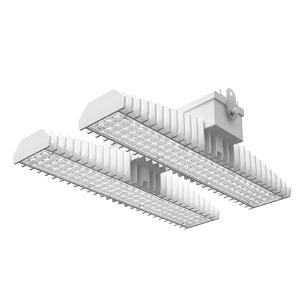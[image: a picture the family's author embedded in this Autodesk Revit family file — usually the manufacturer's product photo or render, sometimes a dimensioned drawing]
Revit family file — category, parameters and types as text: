
# Revit family: 3f_filippi_-_3f_lem_ampio_3f_filippi_-_58882_a0811_-_3f_lem_2_led_100_cr_ampio___vt_6bc2
name_source: partatom
category: Lighting Fixtures
units: mm (PartAtom-declared; Revit-internal decimal feet)

## family parameters
Cut with Voids When Loaded = No
Host = Face
Light Source = No
Part Type = Normal
Room Calculation Point = No
Round Connector Dimension = Use Diameter
Shared = No

## types (1)
- 3F Filippi - 3F LEM Ampio (1 x LED, 15821 lm, 109 W, 4000 K)
    Apparent Load = 109 VA
    Approval mark = CE
    CIE Flux Codes = 60 92 99 100 100
    Color Rendering = 80
    Color Temperature = 4000 K
    Control Gear = Electronic ballast
    Default Elevation = 1800 mm
    Description = Industrial luminaire with high light output and high luminous efficiency designed with the most innovative technologies for environments with temperature up to 55°C.

ILLUMINOTECHNICAL
Luminous efficiency 100% (DLOR 99%, ULOR 1%).
Initial luminous flux of the luminaire 15821 lm.
Direct symmetric wide distribution: the illuminated area has a rectangular shape.
Installation Interdistance Transv.D = 1.58 x hu - Long.D = 1.45 x hu.
Tabular UGR (CIE 117 - 4H-8H; S=0.25H; 70/50/20): RUG 22.2 - 23.2.
Beam angle: 93° - 99°.
Luminous efficacy 145 lm/W.
Lifetime (L93/B10): 30000 h. (tq+25°C)
Lifetime (L90/B10): 50000 h. (tq+25°C)
Lifetime (L85/B10): 80000 h. (tq+25°C)
Lifetime (L80/B10): 100000 h. (tq+25°C)
Lifetime (L85/B10): 50000 h. (tq+55°C)
Sudden decreased luminous flux after 50000 hours: 0% (C0).
Photobiological safety in compliance with IEC/TR 62778: RG0 risk exempt, (IEC 62471).
In compliance with IEC/EN 62722-2-1 - IEC/EN 62717 standards.

SOURCE
2 Mid-Power linear LED modules 50W/840.
Energy efficiency class (UE 2019/2020 - UE 2019/2015): C.
CIE 13.3 Colour rendering index: CRI >80 (R9 <50%).
IES TM-30 Fidelity Index: Rf = 84 Rg = 95.
CCT nominal colour temperature 4000 K.
Colour initial tolerance (MacAdam): SDCM 3.

MECHANICAL
Passive modular heatsinks in die-casted aluminium, painted in white colour.
To optimize the thermal management of the LED module, the heatsinks are oversized and provided with self-cleaning of cooling fins.
Wiring body in aluminium and galvanised steel anchored solidly to the sinks and thermally separated.
3F Lens lenses with high luminous efficiency, transparent methacrylate (PMMA), fixed to the LED modules.
Fixing brackets in stainless steel.
Luminaire with limited surface temperature. - D - (EN 60598-2-24)
Dimensions: 470x542 mm, height 133 mm. Weight 10.119 kg.
IP65 protection degree.
Mechanical strength to impacts IK06 (1 joule).
Glow-wire test resistance 650°C.

ELECTRICAL
Halogen Free electronic wiring 230V-50/60Hz, power factor 0.97, THD <25%, constant output current, class I, 1 driver.
Power of the luminaire 109 W.
ENEC - CE.
SAFE FLICKER: PstLM=<1 and SVM=<0.4 (IEC TR 61547-1 and IEC TR 63158), to ensure a more comfortable and safe light.
Luminaire compliant with EN 60598-2-22 for power supply from a centralised emergency system CPSS (Central Power Supply System), not incorporated in the luminaire - high risk areas excluded. The default power and flux are 100% in AC and 100% in DC.
Ambient temperature from -30°C to +55°C.
Temperature class T6 max 85°C.
Quick connection via M20 3P connector with 9-13 mm tightening range.
Power unit positioned on a separate compartment by the LED module to ensure optimum temperatures of cabling components, to be inspectable and maintainable.
Relative humidity UR: <85%.

INSTALLATION
Ceiling / Suspended / Wall.
All accessories dedicated to this product are available on the Catalog and on our website www.3F-Filippi.com.

ACCESSORIES
A0811 - VT transparent glass, tempered, not flammable, with sealing gasket.
One required for each light module. The pack contains 10 pieces.

APPLICATIONS
In commercial environments, exhibition and industrial areas, stores, open areas.
Applications with high ambient temperature up to 55°C.
Environments in which it is necessary a total protection against falling fragments (eg environments with foodstuffs or machines with moving parts or with extreme temperature changes), use luminaires with polycarbonate lenses.

WARNING
Fixture not suitable for cold stores with an ambient temperature <0°C and/or relative humidity >85%.
Luminaire designed for disposal/recycling at end-of-life.
Replaceable (LED only) light source by a professional. Replaceable control gear by a professional.
    Height = 133 mm  [stored 0.436352 ft]
    Lamp = 1 x LED
    Lamp Light Flux = 15821 lm
    Lamp Power = 109 W
    Lamp count = 1
    Length = 470 mm
    Lifetime = 50000 h
    Luminous efficacy = 145 lm/W
    Manufacturer = 3F Filippi
    ModVariant = No
    Model = 3F Filippi - 58882+A0811 - 3F LEM 2 LED 100 CR AMPIO + VT
    Mounting Place = Ceiling
    Mounting Type = Pendant
    Number of Poles = 1
    OnlyDefault = Yes
    Power Factor = 1
    Product Name = 3F Filippi - 3F LEM Ampio
    Product group = pendant luminaire
    ProductGroupID = 9
    Protection Class = Protection class I
    Protection Degree = IP 65
    RLX_Detail_Level = 1
    RLX_Emergency_Light_Flux = 0 lm
    RLX_Emergency_Type = 0
    RLX_Emergency_Type_DB = No
    RlxData = <blob elided: 102837 chars, md5=d85f1763>
    Socket = socket
    Standby Power = 0 W
    System Light Flux = 15821 lm
    System Power = 109 W
    Type Comments = Product without accessories
    Type Image = 3f_filippi_-_lem_2__a0811.jpg
    URL = http://relux.com
    VarID = ---
    Voltage = 0 V
    Weight = 0.00 kg
    Width = 542 mm

note: [stored X ft] marks values corroborated as IEEE doubles in the binary element streams (Revit-internal decimal feet)

## geometry (parser evidence)
native form markers: Blend x4, Sweep x11
no freeform markers — native parametric forms only
